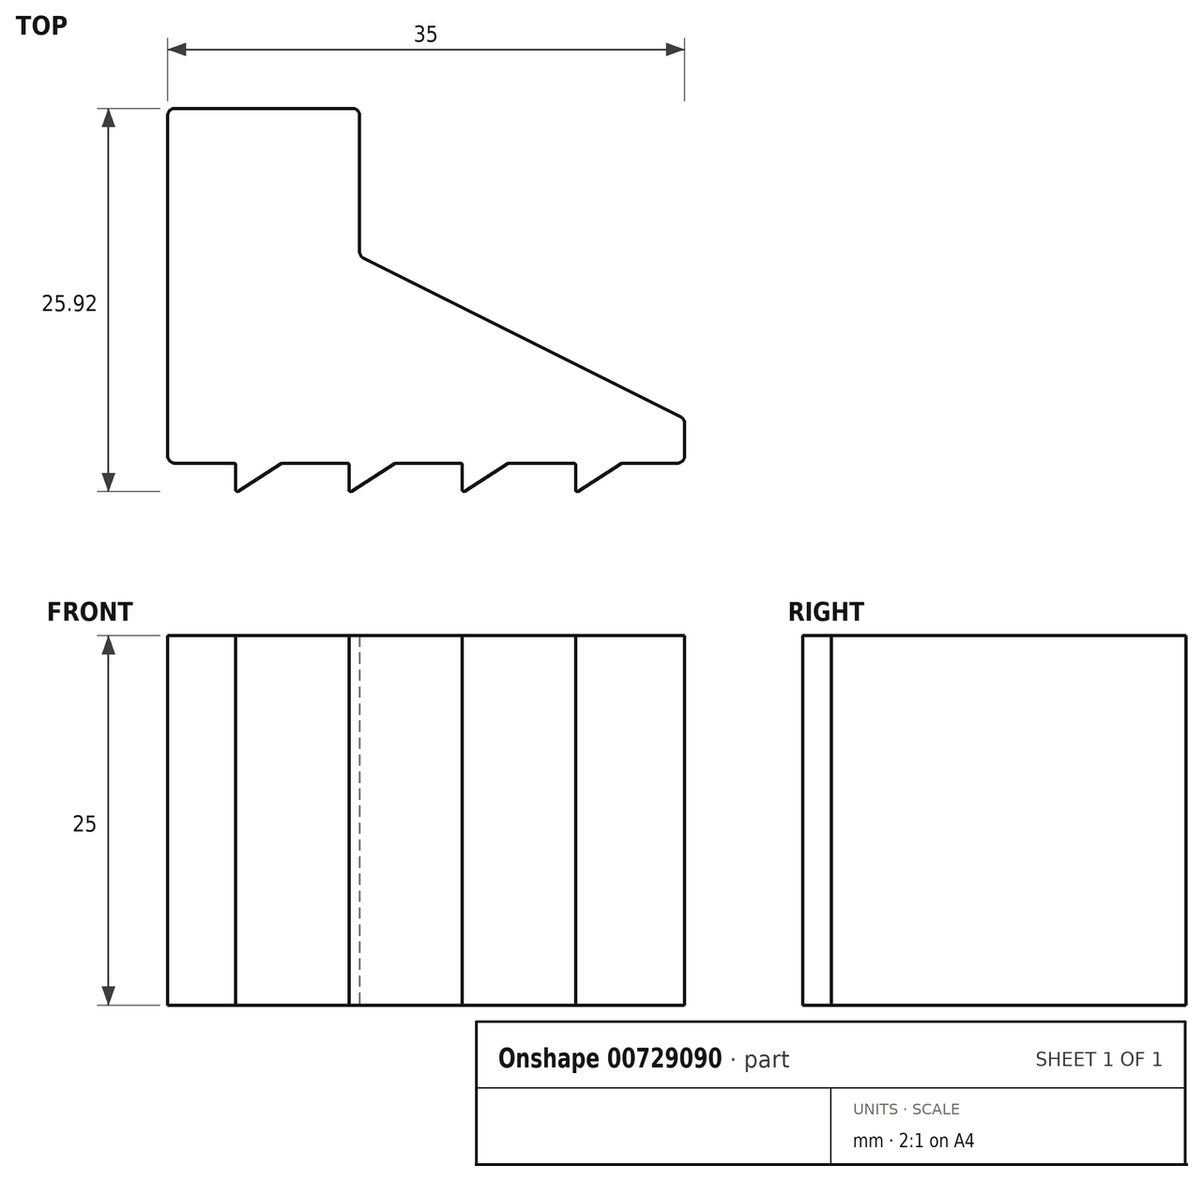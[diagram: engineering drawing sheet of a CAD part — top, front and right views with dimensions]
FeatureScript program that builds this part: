
annotation { "Feature Type Name" : "Feature", "Feature Type Description" : "" }
export const myFeature = defineFeature(function(context is Context, id is Id, definition is map)
    precondition{}
    {
        {
            var Q0;
            Q0=qCreatedBy(makeId("Top.planeOp"),FACE);
            var sketch = newSketch(context, id + "F0", { "sketchPlane" : qUnion([Q0])});
            skLineSegment(sketch, "E0", {"start": v(0, 0.5) * mm, "end": v(0, 23.5) * mm});
            skLineSegment(sketch, "E1", {"start": v(0.5, 24) * mm, "end": v(12.5, 24) * mm});
            skLineSegment(sketch, "E2", {"start": v(13, 23.5) * mm, "end": v(13, 14.3) * mm});
            skLineSegment(sketch, "E3", {"start": v(13.28, 13.86) * mm, "end": v(34.72, 3.14) * mm});
            skLineSegment(sketch, "E4", {"start": v(35, 2.7) * mm, "end": v(35, 0.5) * mm});
            skLineSegment(sketch, "E5", {"start": v(34.5, 0) * mm, "end": v(30.78, 0) * mm});
            skLineSegment(sketch, "E6", {"start": v(4.62, -0.1) * mm, "end": v(4.62, -1.82) * mm});
            skLineSegment(sketch, "E7", {"start": v(4.77, -1.9) * mm, "end": v(7.72, -0.02) * mm});
            skLineSegment(sketch, "E8", {"start": v(27.62, -0.1) * mm, "end": v(27.62, -1.82) * mm});
            skLineSegment(sketch, "E9", {"start": v(27.77, -1.9) * mm, "end": v(30.72, -0.02) * mm});
            skLineSegment(sketch, "E10", {"start": v(12.28, -0.1) * mm, "end": v(12.28, -1.82) * mm});
            skLineSegment(sketch, "E11", {"start": v(12.44, -1.9) * mm, "end": v(15.39, -0.02) * mm});
            skLineSegment(sketch, "E12", {"start": v(19.95, -0.1) * mm, "end": v(19.95, -1.82) * mm});
            skLineSegment(sketch, "E13", {"start": v(20.1, -1.9) * mm, "end": v(23.06, -0.02) * mm});
            skLineSegment(sketch, "E14.trimOffspring", {"start": v(4.52, 0) * mm, "end": v(0.5, 0) * mm});
            skLineSegment(sketch, "E15.trimOffspring", {"start": v(12.18, 0) * mm, "end": v(7.78, 0) * mm});
            skLineSegment(sketch, "E16.trimOffspring", {"start": v(19.85, 0) * mm, "end": v(15.44, 0) * mm});
            skLineSegment(sketch, "E17.trimOffspring", {"start": v(27.52, 0) * mm, "end": v(23.1, 0) * mm});
            skPoint(sketch, "E18.visualSharp", {"position": v(13, 24) * mm});
            skArc(sketch, "E18.filletArc", {"start": v(13, 23.9) * mm, "mid": v(12.97, 23.97) * mm, "end": v(12.9, 24) * mm});
            skPoint(sketch, "E19.visualSharp", {"position": v(4.62, -2) * mm});
            skArc(sketch, "E19.filletArc", {"start": v(4.62, -1.82) * mm, "mid": v(4.67, -1.9) * mm, "end": v(4.77, -1.9) * mm});
            skPoint(sketch, "E20.visualSharp", {"position": v(4.62, 0) * mm});
            skArc(sketch, "E20.filletArc", {"start": v(4.62, -0.1) * mm, "mid": v(4.59, -0.03) * mm, "end": v(4.52, 0) * mm});
            skPoint(sketch, "E21.visualSharp", {"position": v(7.75, 0) * mm});
            skArc(sketch, "E21.filletArc", {"start": v(7.78, 0) * mm, "mid": v(7.75, 0) * mm, "end": v(7.72, -0.02) * mm});
            skPoint(sketch, "E22.visualSharp", {"position": v(12.28, 0) * mm});
            skArc(sketch, "E22.filletArc", {"start": v(12.28, -0.1) * mm, "mid": v(12.25, -0.03) * mm, "end": v(12.18, 0) * mm});
            skPoint(sketch, "E23.visualSharp", {"position": v(12.28, -2) * mm});
            skArc(sketch, "E23.filletArc", {"start": v(12.28, -1.82) * mm, "mid": v(12.34, -1.9) * mm, "end": v(12.44, -1.9) * mm});
            skPoint(sketch, "E24.visualSharp", {"position": v(15.41, 0) * mm});
            skArc(sketch, "E24.filletArc", {"start": v(15.44, 0) * mm, "mid": v(15.41, 0) * mm, "end": v(15.39, -0.02) * mm});
            skPoint(sketch, "E25.visualSharp", {"position": v(19.95, 0) * mm});
            skArc(sketch, "E25.filletArc", {"start": v(19.95, -0.1) * mm, "mid": v(19.92, -0.03) * mm, "end": v(19.85, 0) * mm});
            skPoint(sketch, "E26.visualSharp", {"position": v(19.95, -2) * mm});
            skArc(sketch, "E26.filletArc", {"start": v(19.95, -1.82) * mm, "mid": v(20, -1.9) * mm, "end": v(20.1, -1.9) * mm});
            skPoint(sketch, "E27.visualSharp", {"position": v(23.08, 0) * mm});
            skArc(sketch, "E27.filletArc", {"start": v(23.1, 0) * mm, "mid": v(23.08, 0) * mm, "end": v(23.06, -0.02) * mm});
            skPoint(sketch, "E28.visualSharp", {"position": v(27.62, 0) * mm});
            skArc(sketch, "E28.filletArc", {"start": v(27.62, -0.1) * mm, "mid": v(27.59, -0.03) * mm, "end": v(27.52, 0) * mm});
            skPoint(sketch, "E29.visualSharp", {"position": v(27.62, -2) * mm});
            skArc(sketch, "E29.filletArc", {"start": v(27.62, -1.82) * mm, "mid": v(27.67, -1.9) * mm, "end": v(27.77, -1.9) * mm});
            skPoint(sketch, "E30.visualSharp", {"position": v(30.75, 0) * mm});
            skArc(sketch, "E30.filletArc", {"start": v(30.78, 0) * mm, "mid": v(30.75, 0) * mm, "end": v(30.72, -0.02) * mm});
            skPoint(sketch, "E31.visualSharp", {"position": v(35, 0) * mm});
            skArc(sketch, "E31.filletArc", {"start": v(34.9, 0) * mm, "mid": v(34.97, 0.03) * mm, "end": v(35, 0.1) * mm});
            skPoint(sketch, "E32.visualSharp", {"position": v(35, 3) * mm});
            skArc(sketch, "E32.filletArc", {"start": v(35, 2.7) * mm, "mid": v(34.93, 2.95) * mm, "end": v(34.72, 3.14) * mm});
            skPoint(sketch, "E33.visualSharp", {"position": v(13, 14) * mm});
            skArc(sketch, "E33.filletArc", {"start": v(13, 14.3) * mm, "mid": v(13.07, 14.05) * mm, "end": v(13.28, 13.86) * mm});
            skArc(sketch, "E34.filletArc", {"start": v(13, 23.5) * mm, "mid": v(12.85, 23.85) * mm, "end": v(12.5, 24) * mm});
            skPoint(sketch, "E35.visualSharp", {"position": v(0, 24) * mm});
            skArc(sketch, "E35.filletArc", {"start": v(0.5, 24) * mm, "mid": v(0.15, 23.85) * mm, "end": v(0, 23.5) * mm});
            skPoint(sketch, "E36.visualSharp", {"position": v(0, 0) * mm});
            skArc(sketch, "E36.filletArc", {"start": v(0, 0.5) * mm, "mid": v(0.15, 0.15) * mm, "end": v(0.5, 0) * mm});
            skArc(sketch, "E37.filletArc", {"start": v(34.5, 0) * mm, "mid": v(34.85, 0.15) * mm, "end": v(35, 0.5) * mm});
            skSolve(sketch);
        }
        {
            var Q0;
            Q0=makeQuery(id+"F0.imprint","IMPRINT",FACE,{"disambiguationData":[TD([[makeQuery(id+"F0.imprint","IMPRINT",EDGE,{"derivedFrom":sQuery(id+"F0.wireOp",EDGE,"E0")}),-1.0]])]});
            extrude(context, id + "F1", {"entities" : qUnion([Q0]), "depth" : 25 * mm, "offsetDistance" : 25 * mm});
        }
    });
